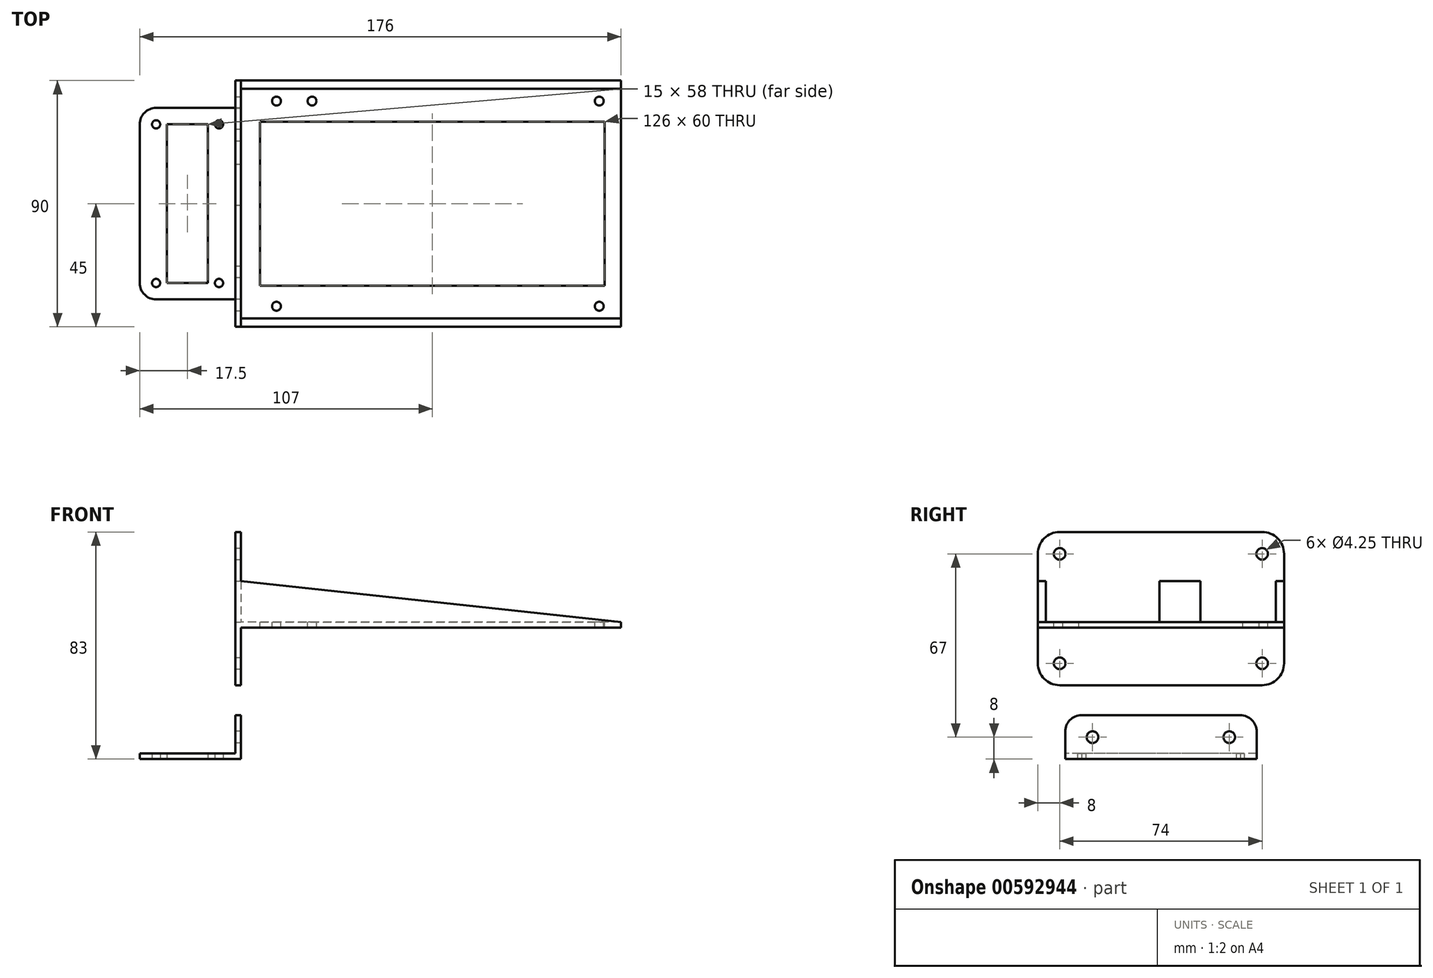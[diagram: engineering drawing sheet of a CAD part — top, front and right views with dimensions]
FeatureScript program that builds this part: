
annotation { "Feature Type Name" : "Feature", "Feature Type Description" : "" }
export const myFeature = defineFeature(function(context is Context, id is Id, definition is map)
    precondition{}
    {
        {
            var Q0;
            Q0=qCreatedBy(makeId("Top.planeOp"),FACE);
            var sketch = newSketch(context, id + "F0", { "sketchPlane" : qUnion([Q0])});
            skLineSegment(sketch, "E0.bottom", {"start": v(-70, 0) * mm, "end": v(68, 0) * mm});
            skLineSegment(sketch, "E0.top", {"start": v(-70, -90) * mm, "end": v(68, -90) * mm});
            skLineSegment(sketch, "E0.left", {"start": v(-70, 0) * mm, "end": v(-70, -90) * mm});
            skLineSegment(sketch, "E0.right", {"start": v(68, 0) * mm, "end": v(68, -90) * mm});
            skPoint(sketch, "E1", {"position": v(-58, -7.5) * mm});
            skPoint(sketch, "E2", {"position": v(-58, -82.5) * mm});
            skPoint(sketch, "E3", {"position": v(-45, -7.5) * mm});
            skPoint(sketch, "E4", {"position": v(-70, -45) * mm});
            skCircle(sketch, "E5", {"center": v(-58, -7.5) * mm, "radius": 1.63 * mm});
            skCircle(sketch, "E6", {"center": v(-45, -7.5) * mm, "radius": 1.63 * mm});
            skCircle(sketch, "E7", {"center": v(-58, -82.5) * mm, "radius": 1.63 * mm});
            skLineSegment(sketch, "E8.bottom", {"start": v(-70, 0) * mm, "end": v(-71, 0) * mm});
            skLineSegment(sketch, "E8.top", {"start": v(-70, -90) * mm, "end": v(-71, -90) * mm});
            skLineSegment(sketch, "E8.right", {"start": v(-71, 0) * mm, "end": v(-71, -90) * mm});
            skPoint(sketch, "E9", {"position": v(-70, -7.5) * mm});
            skLineSegment(sketch, "E10.bottom", {"start": v(-70, 0) * mm, "end": v(0, 0) * mm});
            skLineSegment(sketch, "E10.top", {"start": v(-70, 35) * mm, "end": v(0, 35) * mm});
            skLineSegment(sketch, "E10.left", {"start": v(-70, 0) * mm, "end": v(-70, 35) * mm});
            skLineSegment(sketch, "E10.right", {"start": v(0, 0) * mm, "end": v(0, 35) * mm});
            skLineSegment(sketch, "E11.bottom", {"start": v(-71, 0) * mm, "end": v(-70, 0) * mm});
            skLineSegment(sketch, "E11.top", {"start": v(-71, 35) * mm, "end": v(-70, 35) * mm});
            skLineSegment(sketch, "E11.left", {"start": v(-71, 0) * mm, "end": v(-71, 35) * mm});
            skPoint(sketch, "E12", {"position": v(-64, 29) * mm});
            skPoint(sketch, "E13", {"position": v(-64, 6) * mm});
            skPoint(sketch, "E14", {"position": v(-6, 29) * mm});
            skPoint(sketch, "E15", {"position": v(-6, 6) * mm});
            skCircle(sketch, "E16", {"center": v(-64, 29) * mm, "radius": 1.5 * mm});
            skCircle(sketch, "E17", {"center": v(-6, 29) * mm, "radius": 1.5 * mm});
            skCircle(sketch, "E18", {"center": v(-6, 6) * mm, "radius": 1.5 * mm});
            skCircle(sketch, "E19", {"center": v(-64, 6) * mm, "radius": 1.5 * mm});
            skPoint(sketch, "E20", {"position": v(-70, 17.5) * mm});
            skLineSegment(sketch, "E21.bottom", {"start": v(-64, -75) * mm, "end": v(62, -75) * mm});
            skLineSegment(sketch, "E21.top", {"start": v(-64, -15) * mm, "end": v(62, -15) * mm});
            skLineSegment(sketch, "E21.left", {"start": v(-64, -15) * mm, "end": v(-64, -75) * mm});
            skLineSegment(sketch, "E21.right", {"start": v(62, -15) * mm, "end": v(62, -75) * mm});
            skLineSegment(sketch, "E22.bottom", {"start": v(-64, 12) * mm, "end": v(-6, 12) * mm});
            skLineSegment(sketch, "E22.top", {"start": v(-64, 23) * mm, "end": v(-6, 23) * mm});
            skLineSegment(sketch, "E22.left", {"start": v(-64, 23) * mm, "end": v(-64, 12) * mm});
            skLineSegment(sketch, "E22.right", {"start": v(-6, 23) * mm, "end": v(-6, 12) * mm});
            skPoint(sketch, "E23", {"position": v(-64, -45) * mm});
            skLineSegment(sketch, "E24", {"start": v(-70, -45) * mm, "end": v(-64, -45) * mm, "construction": true});
            skLineSegment(sketch, "E25", {"start": v(62, -45) * mm, "end": v(68, -45) * mm, "construction": true});
            skPoint(sketch, "E26", {"position": v(-64, 17.5) * mm});
            skPoint(sketch, "E27", {"position": v(-35, 35) * mm});
            skPoint(sketch, "E28", {"position": v(-35, 12) * mm});
            skLineSegment(sketch, "E29", {"start": v(-58, -82.5) * mm, "end": v(-58, -90) * mm, "construction": true});
            skLineSegment(sketch, "E30", {"start": v(-58, -90) * mm, "end": v(-58, -82.5) * mm, "construction": true});
            skLineSegment(sketch, "E31", {"start": v(-58, -75) * mm, "end": v(-58, -82.5) * mm, "construction": true});
            skLineSegment(sketch, "E32", {"start": v(-6, 29) * mm, "end": v(-6, 35) * mm, "construction": true});
            skLineSegment(sketch, "E33", {"start": v(-6, 23) * mm, "end": v(-6, 29) * mm, "construction": true});
            skLineSegment(sketch, "E34", {"start": v(-6, 12) * mm, "end": v(-6, 6) * mm, "construction": true});
            skPoint(sketch, "E35", {"position": v(60, -7.5) * mm});
            skPoint(sketch, "E36", {"position": v(60, -82.5) * mm});
            skCircle(sketch, "E37", {"center": v(60, -7.5) * mm, "radius": 1.63 * mm});
            skCircle(sketch, "E38", {"center": v(60, -82.5) * mm, "radius": 1.63 * mm});
            skSolve(sketch);
        }
        {
            var Q0;
            Q0=makeQuery(id+"F0.imprint","IMPRINT",FACE,{"disambiguationData":[TD([[makeQuery(id+"F0.imprint","IMPRINT",EDGE,{"derivedFrom":sQuery(id+"F0.wireOp",EDGE,"E0.left")}),-1.0]])]});
            var Q1;
            {var subQ0=sQuery(id+"F0.wireOp",EDGE,"E0.left");Q1=makeQuery(id+"F0.imprint","IMPRINT",FACE,{"disambiguationData":[TD([[makeQuery(id+"F0.imprint","IMPRINT",EDGE,{"derivedFrom":subQ0}),1.0]])]});}
            extrude(context, id + "F1", {"entities" : qUnion([Q0, Q1]), "oppositeDirection" : true, "depth" : 2 * mm, "offsetDistance" : 25 * mm});
        }
        {
            var Q0;
            Q0=makeQuery(id+"F1.opExtrude","SWEPT_FACE",FACE,{"disambiguationData":[OSD([sQuery(id+"F0.wireOp",EDGE,"E8.right")])]});
            var sketch = newSketch(context, id + "F2", { "sketchPlane" : qUnion([Q0])});
            skLineSegment(sketch, "E39.bottom", {"start": v(0, 33) * mm, "end": v(90, 33) * mm});
            skLineSegment(sketch, "E39.top", {"start": v(0, -23) * mm, "end": v(90, -23) * mm});
            skLineSegment(sketch, "E39.left", {"start": v(0, 33) * mm, "end": v(0, -23) * mm});
            skLineSegment(sketch, "E39.right", {"start": v(90, 33) * mm, "end": v(90, -23) * mm});
            skPoint(sketch, "E40", {"position": v(8, 25) * mm});
            skPoint(sketch, "E41", {"position": v(8, -15) * mm});
            skPoint(sketch, "E42", {"position": v(82, -15) * mm});
            skPoint(sketch, "E43", {"position": v(82, 25) * mm});
            skCircle(sketch, "E44", {"center": v(8, 25) * mm, "radius": 2.12 * mm});
            skCircle(sketch, "E45", {"center": v(82, 25) * mm, "radius": 2.12 * mm});
            skCircle(sketch, "E46", {"center": v(82, -15) * mm, "radius": 2.12 * mm});
            skCircle(sketch, "E47", {"center": v(8, -15) * mm, "radius": 2.12 * mm});
            skLineSegment(sketch, "E48.bottom", {"start": v(30.5, 15) * mm, "end": v(45.5, 15) * mm});
            skLineSegment(sketch, "E48.top", {"start": v(30.5, 0) * mm, "end": v(45.5, 0) * mm});
            skLineSegment(sketch, "E48.left", {"start": v(30.5, 15) * mm, "end": v(30.5, 0) * mm});
            skLineSegment(sketch, "E48.right", {"start": v(45.5, 15) * mm, "end": v(45.5, 0) * mm});
            skPoint(sketch, "E49", {"position": v(7.5, 0) * mm});
            skCircle(sketch, "E50", {"center": v(-17.5, 8) * mm, "radius": 6 * mm});
            skLineSegment(sketch, "E51", {"start": v(0, -5) * mm, "end": v(90, -5) * mm, "construction": true});
            skLineSegment(sketch, "E52", {"start": v(0, 15) * mm, "end": v(90, 15) * mm, "construction": true});
            skLineSegment(sketch, "E53.bottom", {"start": v(-27.5, 3) * mm, "end": v(-7.5, 3) * mm});
            skLineSegment(sketch, "E53.top", {"start": v(-27.5, 0) * mm, "end": v(-7.5, 0) * mm});
            skLineSegment(sketch, "E53.left", {"start": v(-27.5, 3) * mm, "end": v(-27.5, 0) * mm});
            skLineSegment(sketch, "E53.right", {"start": v(-7.5, 3) * mm, "end": v(-7.5, 0) * mm});
            skPoint(sketch, "E54", {"position": v(-17.5, 3) * mm});
            skLineSegment(sketch, "E55", {"start": v(-23.5, 8) * mm, "end": v(-23.5, 3) * mm});
            skLineSegment(sketch, "E56", {"start": v(-11.5, 8) * mm, "end": v(-11.5, 3) * mm});
            skSolve(sketch);
        }
        {
            var Q0;
            {var subQ0=sQuery(id+"F2.wireOp",EDGE,"E39.bottom");Q0=makeQuery(id+"F2.imprint","IMPRINT",FACE,{"disambiguationData":[TD([[makeQuery(id+"F2.imprint","IMPRINT",EDGE,{"derivedFrom":subQ0}),-1.0]])]});}
            var Q1;
            {var subQ1=sQuery(id+"F0.wireOp",EDGE,"E0.left");var subQ2=makeQuery(id+"F1.opExtrude","CAP_EDGE",EDGE,{"disambiguationData":[OSD([subQ1])],"isStart":true});Q1=makeQuery(id+"F2.imprint","IMPRINT",FACE,{"disambiguationData":[TD([[makeQuery(id+"F2.imprint","IMPRINT",EDGE,{"derivedFrom":subQ2}),-1.0]])]});}
            var Q2;
            {var subQ0=sQuery(id+"F2.wireOp",EDGE,"E39.top");Q2=makeQuery(id+"F2.imprint","IMPRINT",FACE,{"disambiguationData":[TD([[makeQuery(id+"F2.imprint","IMPRINT",EDGE,{"derivedFrom":subQ0}),1.0]])]});}
            var Q3;
            {var subQ1=sQuery(id+"F0.wireOp",EDGE,"E8.right");var subQ2=makeQuery(id+"F1.opExtrude","CAP_EDGE",EDGE,{"disambiguationData":[OSD([subQ1])],"isStart":true});Q3=makeQuery(id+"F2.imprint","IMPRINT",FACE,{"disambiguationData":[TD([[makeQuery(id+"F2.imprint","IMPRINT",EDGE,{"derivedFrom":subQ2}),-1.0]])]});}
            var Q4;
            Q4=makeQuery(id+"F2.imprint","IMPRINT",FACE,{"disambiguationData":[TD([[makeQuery(id+"F2.imprint","IMPRINT",EDGE,{"derivedFrom":sQuery(id+"F2.wireOp",EDGE,"BuqxCLef-Ckgz-Im7e-t12U-0kkfHIVaMpYe.bottom")}),1.0]])]});
            var Q5;
            Q5=makeQuery(id+"F2.imprint","IMPRINT",FACE,{"disambiguationData":[TD([[makeQuery(id+"F2.imprint","IMPRINT",EDGE,{"derivedFrom":sQuery(id+"F2.wireOp",EDGE,"ZPSCuZf2-8GBL-TR2S-GhvN-7OaKN75D86po.bottom")}),1.0]])]});
            extrude(context, id + "F3", {"entities" : qUnion([Q0, Q1, Q2, Q3, Q4, Q5]), "operationType" : NewBodyOperationType.ADD, "depth" : 2 * mm, "offsetDistance" : 25 * mm});
        }
        {
            var Q0;
            Q0=makeQuery(id+"F3.opExtrude","SWEPT_EDGE",EDGE,{"disambiguationData":[OSD([sQuery(id+"F2.wireOp",EDGE,"E39.bottom"),sQuery(id+"F2.wireOp",EDGE,"E39.right")])]});
            var Q1;
            Q1=makeQuery(id+"F3.opExtrude","SWEPT_EDGE",EDGE,{"disambiguationData":[OSD([sQuery(id+"F2.wireOp",EDGE,"E39.top"),sQuery(id+"F2.wireOp",EDGE,"E39.right")])]});
            var Q2;
            Q2=makeQuery(id+"F3.opExtrude","SWEPT_EDGE",EDGE,{"disambiguationData":[OSD([sQuery(id+"F2.wireOp",EDGE,"E39.top"),sQuery(id+"F2.wireOp",EDGE,"E39.left")])]});
            var Q3;
            Q3=makeQuery(id+"F3.opExtrude","SWEPT_EDGE",EDGE,{"disambiguationData":[OSD([sQuery(id+"F2.wireOp",EDGE,"E39.bottom"),sQuery(id+"F2.wireOp",EDGE,"E39.left")])]});
            fillet(context, id + "F4", {"entities" : qUnion([Q0, Q1, Q2, Q3]), "tangentPropagation" : true, "radius" : 8 * mm, "defaultsChanged" : false, "vertexSettings" : [], "allowEdgeOverflow" : false});
        }
        {
            var Q0;
            {var subQ2=sQuery(id+"F2.wireOp",EDGE,"E39.bottom");Q0=makeQuery(id+"F2.imprint","IMPRINT",FACE,{"disambiguationData":[TD([[makeQuery(id+"F2.imprint","IMPRINT",EDGE,{"derivedFrom":subQ2}),-1.0]])]});}
            var sketch = newSketch(context, id + "F5", { "sketchPlane" : qUnion([Q0])});
            skLineSegment(sketch, "E57.bottom", {"start": v(90, 15) * mm, "end": v(87, 15) * mm});
            skLineSegment(sketch, "E57.top", {"start": v(90, 0) * mm, "end": v(87, 0) * mm});
            skLineSegment(sketch, "E57.left", {"start": v(90, 15) * mm, "end": v(90, 0) * mm});
            skLineSegment(sketch, "E57.right", {"start": v(87, 15) * mm, "end": v(87, 0) * mm});
            skLineSegment(sketch, "E58.bottom", {"start": v(3, 15) * mm, "end": v(0, 15) * mm});
            skLineSegment(sketch, "E58.top", {"start": v(3, 0) * mm, "end": v(0, 0) * mm});
            skLineSegment(sketch, "E58.left", {"start": v(3, 15) * mm, "end": v(3, 0) * mm});
            skLineSegment(sketch, "E58.right", {"start": v(0, 15) * mm, "end": v(0, 0) * mm});
            skSolve(sketch);
        }
        {
            var Q0;
            Q0=makeQuery(id+"F5.imprint","IMPRINT",FACE,{"disambiguationData":[TD([[makeQuery(id+"F5.imprint","IMPRINT",EDGE,{"derivedFrom":sQuery(id+"F5.wireOp",EDGE,"E57.bottom")}),1.0]])]});
            var Q1;
            Q1=makeQuery(id+"F5.imprint","IMPRINT",FACE,{"disambiguationData":[TD([[makeQuery(id+"F5.imprint","IMPRINT",EDGE,{"derivedFrom":sQuery(id+"F5.wireOp",EDGE,"E58.bottom")}),1.0]])]});
            extrude(context, id + "F6", {"entities" : qUnion([Q0, Q1]), "operationType" : NewBodyOperationType.ADD, "oppositeDirection" : true, "depth" : 139 * mm, "offsetDistance" : 25 * mm});
        }
        {
            var Q0;
            Q0=makeQuery(id+"F6.opExtrude","CAP_EDGE",EDGE,{"disambiguationData":[OSD([sQuery(id+"F5.wireOp",EDGE,"E57.bottom")])],"isStart":false});
            var Q1;
            Q1=makeQuery(id+"F6.opExtrude","CAP_EDGE",EDGE,{"disambiguationData":[OSD([sQuery(id+"F5.wireOp",EDGE,"E58.bottom")])],"isStart":false});
            chamfer(context, id + "F7", {"entities" : qUnion([Q0, Q1]), "chamferType" : ChamferType.TWO_OFFSETS, "width1" : 139 * mm, "oppositeDirection" : false, "width2" : 15 * mm, "tangentPropagation" : true});
        }
        {
            var Q0;
            Q0=makeQuery(id+"F3.boolean.opBoolean","MERGE",FACE,{"derivedFrom":[makeQuery(id+"F1.opExtrude","CAP_FACE",FACE,{"disambiguationData":[OSD([sQuery(id+"F0.wireOp",EDGE,"E0.bottom"),sQuery(id+"F0.wireOp",EDGE,"E0.top"),sQuery(id+"F0.wireOp",EDGE,"E0.right"),sQuery(id+"F0.wireOp",EDGE,"E5"),sQuery(id+"F0.wireOp",EDGE,"E6"),sQuery(id+"F0.wireOp",EDGE,"E7"),sQuery(id+"F0.wireOp",EDGE,"E8.bottom"),sQuery(id+"F0.wireOp",EDGE,"E8.top"),sQuery(id+"F0.wireOp",EDGE,"E8.right"),sQuery(id+"F0.wireOp",EDGE,"E21.bottom"),sQuery(id+"F0.wireOp",EDGE,"E21.top"),sQuery(id+"F0.wireOp",EDGE,"E21.left"),sQuery(id+"F0.wireOp",EDGE,"E21.right"),sQuery(id+"F0.wireOp",EDGE,"E37"),sQuery(id+"F0.wireOp",EDGE,"E38")])],"isStart":true}),makeQuery(id+"F3.opExtrude","SWEPT_FACE",FACE,{"disambiguationData":[OSD([sQuery(id+"F2.wireOp",EDGE,"E48.top")])]})]});
            cPlane(context, id + "F8", {"entities" : qUnion([Q0]), "cplaneType" : CPlaneType.OFFSET, "offset" : 50 * mm, "oppositeDirection" : true, "width" : 150 * mm, "height" : 150 * mm});
        }
        {
            var Q0;
            Q0=qCreatedBy(id+"F8.planeOp",FACE);
            var sketch = newSketch(context, id + "F9", { "sketchPlane" : qUnion([Q0])});
            skLineSegment(sketch, "E59.bottom", {"start": v(-108, -10) * mm, "end": v(-73, -10) * mm});
            skLineSegment(sketch, "E59.top", {"start": v(-108, -80) * mm, "end": v(-73, -80) * mm});
            skLineSegment(sketch, "E59.left", {"start": v(-108, -10) * mm, "end": v(-108, -80) * mm});
            skLineSegment(sketch, "E59.right", {"start": v(-73, -10) * mm, "end": v(-73, -80) * mm});
            skPoint(sketch, "E60", {"position": v(-73, -45) * mm});
            skPoint(sketch, "E61", {"position": v(-102, -16) * mm});
            skPoint(sketch, "E62", {"position": v(-79, -16) * mm});
            skPoint(sketch, "E63", {"position": v(-102, -74) * mm});
            skPoint(sketch, "E64", {"position": v(-79, -74) * mm});
            skLineSegment(sketch, "E65.bottom", {"start": v(-102, -16) * mm, "end": v(-79, -16) * mm, "construction": true});
            skLineSegment(sketch, "E65.top", {"start": v(-102, -74) * mm, "end": v(-79, -74) * mm, "construction": true});
            skLineSegment(sketch, "E65.left", {"start": v(-102, -16) * mm, "end": v(-102, -74) * mm, "construction": true});
            skLineSegment(sketch, "E65.right", {"start": v(-79, -16) * mm, "end": v(-79, -74) * mm, "construction": true});
            skPoint(sketch, "E66", {"position": v(-79, -45) * mm});
            skPoint(sketch, "E67", {"position": v(-90.5, -10) * mm});
            skPoint(sketch, "E68", {"position": v(-90.5, -16) * mm});
            skCircle(sketch, "E69", {"center": v(-102, -16) * mm, "radius": 1.5 * mm});
            skCircle(sketch, "E70", {"center": v(-79, -16) * mm, "radius": 1.5 * mm});
            skCircle(sketch, "E71", {"center": v(-79, -74) * mm, "radius": 1.5 * mm});
            skCircle(sketch, "E72", {"center": v(-102, -74) * mm, "radius": 1.5 * mm});
            skLineSegment(sketch, "E73.bottom", {"start": v(-98, -16) * mm, "end": v(-83, -16) * mm});
            skLineSegment(sketch, "E73.top", {"start": v(-98, -74) * mm, "end": v(-83, -74) * mm});
            skLineSegment(sketch, "E73.left", {"start": v(-98, -16) * mm, "end": v(-98, -74) * mm});
            skLineSegment(sketch, "E73.right", {"start": v(-83, -16) * mm, "end": v(-83, -74) * mm});
            skPoint(sketch, "E74", {"position": v(-90.5, -74) * mm});
            skSolve(sketch);
        }
        {
            var Q0;
            Q0=makeQuery(id+"F9.imprint","IMPRINT",FACE,{"disambiguationData":[TD([[makeQuery(id+"F9.imprint","IMPRINT",EDGE,{"derivedFrom":sQuery(id+"F9.wireOp",EDGE,"E59.bottom")}),-1.0]])]});
            extrude(context, id + "F10", {"entities" : qUnion([Q0]), "operationType" : NewBodyOperationType.ADD, "depth" : 2 * mm, "offsetDistance" : 25 * mm});
        }
        {
            var Q0;
            Q0=makeQuery(id+"F10.opExtrude","SWEPT_FACE",FACE,{"disambiguationData":[OSD([sQuery(id+"F9.wireOp",EDGE,"E59.right")])]});
            var sketch = newSketch(context, id + "F11", { "sketchPlane" : qUnion([Q0])});
            skLineSegment(sketch, "E75.bottom", {"start": v(-80, -50) * mm, "end": v(-10, -50) * mm});
            skLineSegment(sketch, "E75.top", {"start": v(-80, -34) * mm, "end": v(-10, -34) * mm});
            skLineSegment(sketch, "E75.left", {"start": v(-80, -50) * mm, "end": v(-80, -34) * mm});
            skLineSegment(sketch, "E75.right", {"start": v(-10, -50) * mm, "end": v(-10, -34) * mm});
            skCircle(sketch, "E76", {"center": v(-70, -42) * mm, "radius": 2.12 * mm});
            skCircle(sketch, "E77", {"center": v(-20, -42) * mm, "radius": 2.12 * mm});
            skSolve(sketch);
        }
        {
            var Q0;
            {var subQ2=sQuery(id+"F11.wireOp",EDGE,"E75.top");Q0=makeQuery(id+"F11.imprint","IMPRINT",FACE,{"disambiguationData":[TD([[makeQuery(id+"F11.imprint","IMPRINT",EDGE,{"derivedFrom":subQ2}),-1.0]])]});}
            var Q1;
            {var subQ0=sQuery(id+"F11.wireOp",EDGE,"E75.bottom");Q1=makeQuery(id+"F11.imprint","IMPRINT",FACE,{"disambiguationData":[TD([[makeQuery(id+"F11.imprint","IMPRINT",EDGE,{"derivedFrom":subQ0}),-1.0]])]});}
            extrude(context, id + "F12", {"entities" : qUnion([Q0, Q1]), "operationType" : NewBodyOperationType.ADD, "depth" : 2 * mm, "offsetDistance" : 25 * mm});
        }
        {
            var Q0;
            Q0=makeQuery(id+"F10.opExtrude","SWEPT_EDGE",EDGE,{"disambiguationData":[OSD([sQuery(id+"F9.wireOp",EDGE,"E59.bottom"),sQuery(id+"F9.wireOp",EDGE,"E59.left")])]});
            var Q1;
            Q1=makeQuery(id+"F10.opExtrude","SWEPT_EDGE",EDGE,{"disambiguationData":[OSD([sQuery(id+"F9.wireOp",EDGE,"E59.top"),sQuery(id+"F9.wireOp",EDGE,"E59.left")])]});
            var Q2;
            Q2=makeQuery(id+"F12.opExtrude","SWEPT_EDGE",EDGE,{"disambiguationData":[OSD([sQuery(id+"F11.wireOp",EDGE,"E75.top"),sQuery(id+"F11.wireOp",EDGE,"E75.left")])]});
            var Q3;
            Q3=makeQuery(id+"F12.opExtrude","SWEPT_EDGE",EDGE,{"disambiguationData":[OSD([sQuery(id+"F11.wireOp",EDGE,"E75.top"),sQuery(id+"F11.wireOp",EDGE,"E75.right")])]});
            fillet(context, id + "F13", {"entities" : qUnion([Q0, Q1, Q2, Q3]), "tangentPropagation" : true, "radius" : 6 * mm, "defaultsChanged" : false, "vertexSettings" : [], "allowEdgeOverflow" : false});
        }
    });
